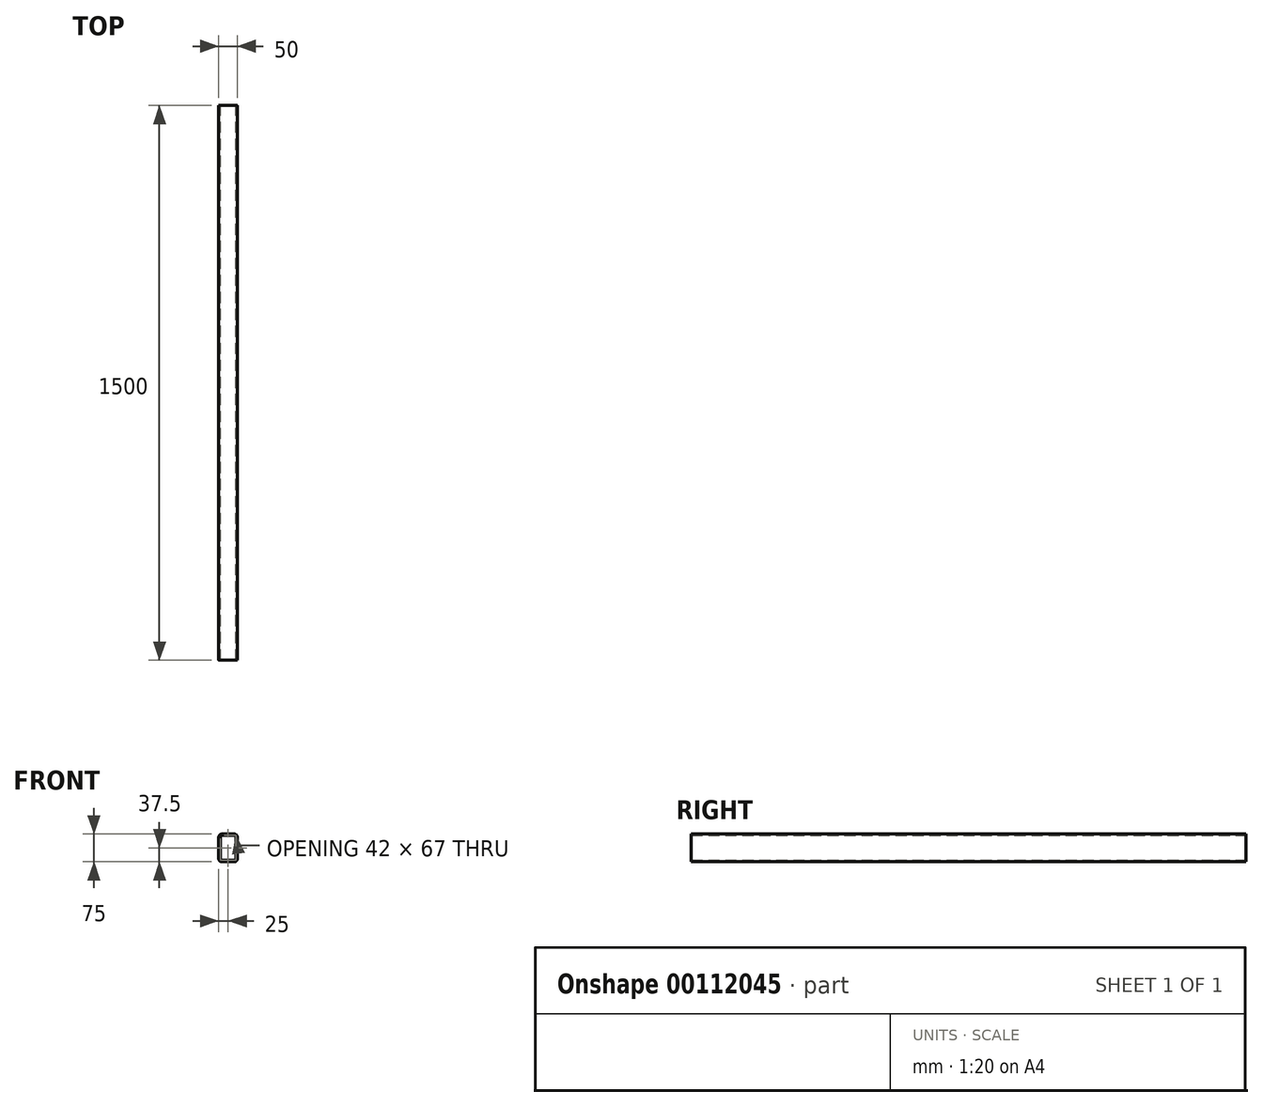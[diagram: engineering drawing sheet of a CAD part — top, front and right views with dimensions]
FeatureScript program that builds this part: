
annotation { "Feature Type Name" : "Feature", "Feature Type Description" : "" }
export const myFeature = defineFeature(function(context is Context, id is Id, definition is map)
    precondition{}
    {
        {
            var Q0;
            Q0=qCreatedBy(makeId("Front.planeOp"),FACE);
            var sketch = newSketch(context, id + "F0", { "sketchPlane" : qUnion([Q0])});
            skLineSegment(sketch, "E0.bottom", {"start": v(17, 37.5) * mm, "end": v(-17, 37.5) * mm});
            skLineSegment(sketch, "E0.top", {"start": v(17, -37.5) * mm, "end": v(-17, -37.5) * mm});
            skLineSegment(sketch, "E0.left", {"start": v(25, 29.5) * mm, "end": v(25, -29.5) * mm});
            skLineSegment(sketch, "E0.right", {"start": v(-25, 29.5) * mm, "end": v(-25, -29.5) * mm});
            skPoint(sketch, "E0.middle", {"position": v(0, 0) * mm});
            skPoint(sketch, "E1.visualSharp", {"position": v(-25, 37.5) * mm});
            skArc(sketch, "E1.filletArc", {"start": v(-17, 37.5) * mm, "mid": v(-22.66, 35.16) * mm, "end": v(-25, 29.5) * mm});
            skPoint(sketch, "E2.visualSharp", {"position": v(25, 37.5) * mm});
            skArc(sketch, "E2.filletArc", {"start": v(25, 29.5) * mm, "mid": v(22.66, 35.16) * mm, "end": v(17, 37.5) * mm});
            skPoint(sketch, "E3.visualSharp", {"position": v(-25, -37.5) * mm});
            skArc(sketch, "E3.filletArc", {"start": v(-25, -29.5) * mm, "mid": v(-22.66, -35.16) * mm, "end": v(-17, -37.5) * mm});
            skPoint(sketch, "E4.visualSharp", {"position": v(25, -37.5) * mm});
            skArc(sketch, "E4.filletArc", {"start": v(17, -37.5) * mm, "mid": v(22.66, -35.16) * mm, "end": v(25, -29.5) * mm});
            skArc(sketch, "E5.0", {"start": v(-17, 33.5) * mm, "mid": v(-19.83, 32.33) * mm, "end": v(-21, 29.5) * mm});
            skLineSegment(sketch, "E5.1", {"start": v(17, 33.5) * mm, "end": v(-17, 33.5) * mm});
            skLineSegment(sketch, "E5.2", {"start": v(-21, 29.5) * mm, "end": v(-21, -29.5) * mm});
            skArc(sketch, "E5.3", {"start": v(21, 29.5) * mm, "mid": v(19.83, 32.33) * mm, "end": v(17, 33.5) * mm});
            skArc(sketch, "E5.4", {"start": v(-21, -29.5) * mm, "mid": v(-19.83, -32.33) * mm, "end": v(-17, -33.5) * mm});
            skLineSegment(sketch, "E5.5", {"start": v(17, -33.5) * mm, "end": v(-17, -33.5) * mm});
            skArc(sketch, "E5.6", {"start": v(17, -33.5) * mm, "mid": v(19.83, -32.33) * mm, "end": v(21, -29.5) * mm});
            skLineSegment(sketch, "E5.7", {"start": v(21, 29.5) * mm, "end": v(21, -29.5) * mm});
            skSolve(sketch);
        }
        {
            var Q0;
            Q0=qSketchRegion(id+"F0",true);
            extrude(context, id + "F1", {"entities" : qUnion([Q0]), "depth" : 1500 * mm});
        }
    });
